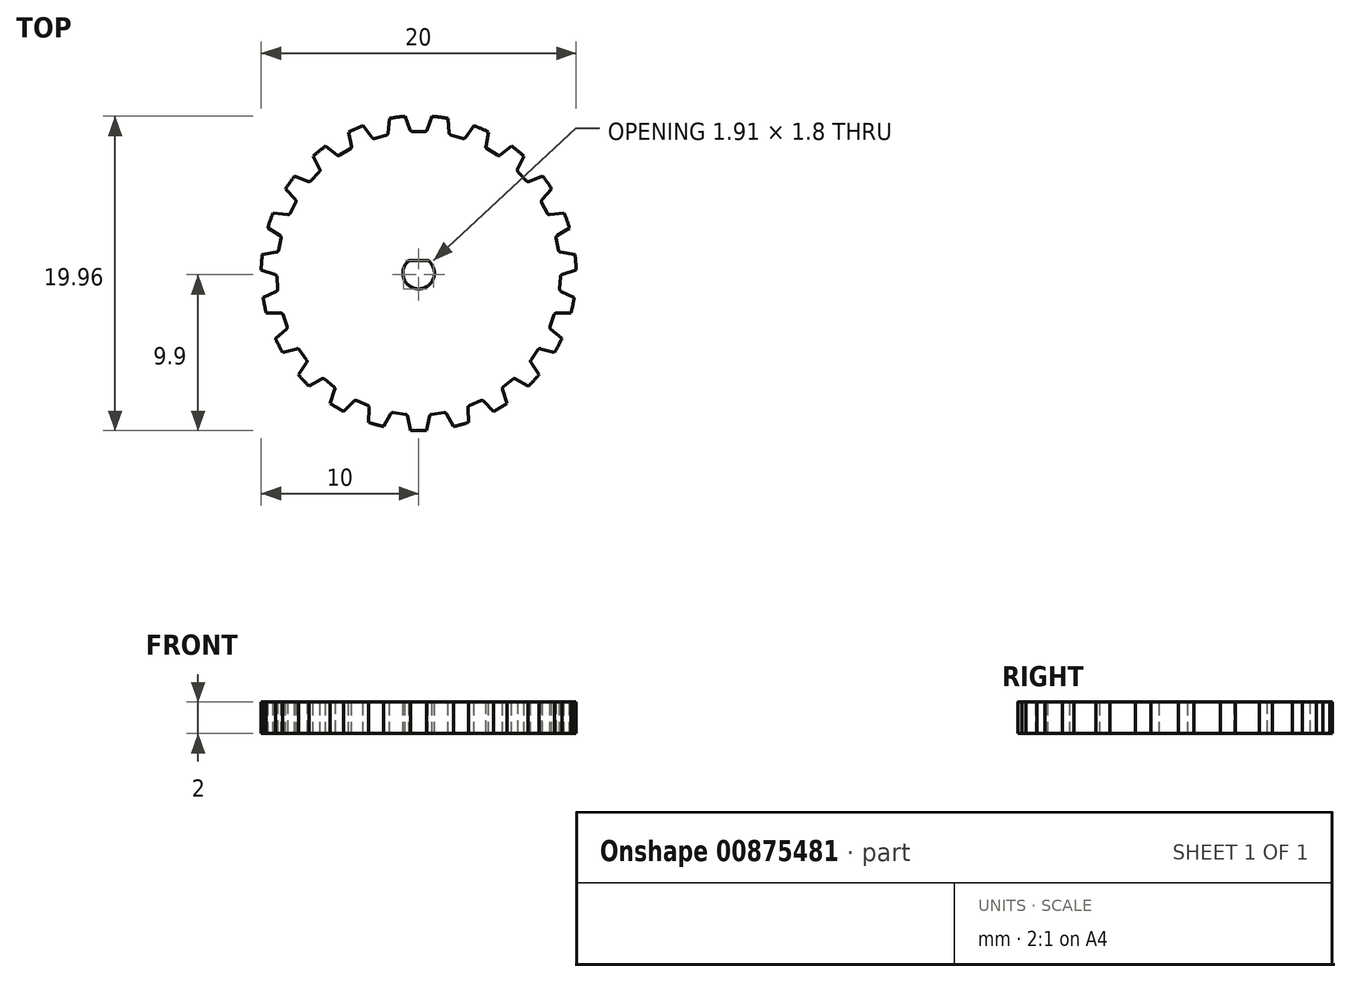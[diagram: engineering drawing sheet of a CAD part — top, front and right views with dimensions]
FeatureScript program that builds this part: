
annotation { "Feature Type Name" : "Feature", "Feature Type Description" : "" }
export const myFeature = defineFeature(function(context is Context, id is Id, definition is map)
    precondition{}
    {
        {
            var Q0;
            Q0=qCreatedBy(makeId("Top.planeOp"),FACE);
            var sketch = newSketch(context, id + "F0", { "sketchPlane" : qUnion([Q0])});
            skCircle(sketch, "E0", {"center": v(0, 0) * mm, "radius": 10 * mm});
            skSolve(sketch);
        }
        {
            var Q0;
            Q0 = qSketchRegion(id + "F0", true);
            extrude(context, id + "F1", {"entities" : qUnion([Q0]), "depth" : 2 * mm, "offsetDistance" : 25 * mm});
        }
        {
            var Q0;
            Q0=makeQuery(id+"F1.opExtrude","CAP_FACE",FACE,{"disambiguationData":[OSD([sQuery(id+"F0.wireOp",EDGE,"E0")])],"isStart":false});
            var sketch = newSketch(context, id + "F2", { "sketchPlane" : qUnion([Q0])});
            skLineSegment(sketch, "E1", {"start": v(0, 0) * mm, "end": v(0, 9) * mm});
            skLineSegment(sketch, "E2", {"start": v(0, 9) * mm, "end": v(0.5, 9) * mm});
            skLineSegment(sketch, "E3", {"start": v(0, 9) * mm, "end": v(0, 10) * mm});
            skLineSegment(sketch, "E4", {"start": v(0, 10) * mm, "end": v(0.88, 10) * mm});
            skLineSegment(sketch, "E5", {"start": v(0.88, 10) * mm, "end": v(0.5, 9) * mm});
            skLineSegment(sketch, "E6.MirrorCS", {"start": v(0, 10) * mm, "end": v(-0.88, 10) * mm});
            skLineSegment(sketch, "E7.MirrorCS", {"start": v(-0.88, 10) * mm, "end": v(-0.5, 9) * mm});
            skLineSegment(sketch, "E8.MirrorCS", {"start": v(0, 9) * mm, "end": v(-0.5, 9) * mm});
            skSolve(sketch);
        }
        {
            var Q0;
            {var subQ0=sQuery(id+"F2.wireOp",EDGE,"E2");Q0=makeQuery(id+"F2.imprint","IMPRINT",FACE,{"disambiguationData":[TD([[makeQuery(id+"F2.imprint","IMPRINT",EDGE,{"derivedFrom":subQ0}),1.0]])]});}
            var Q1;
            {var subQ0=sQuery(id+"F2.wireOp",EDGE,"E3");Q1=makeQuery(id+"F2.imprint","IMPRINT",FACE,{"disambiguationData":[TD([[makeQuery(id+"F2.imprint","IMPRINT",EDGE,{"derivedFrom":subQ0}),1.0]])]});}
            extrude(context, id + "F3", {"entities" : qUnion([Q0, Q1]), "operationType" : NewBodyOperationType.REMOVE, "oppositeDirection" : true, "depth" : 25 * mm, "offsetDistance" : 25 * mm});
        }
        {
            var Q0;
            Q0=makeQuery(id+"F3.boolean.opBoolean","COPY",FACE,{"derivedFrom":makeQuery(id+"F3.opExtrude","SWEPT_FACE",FACE,{"disambiguationData":[OSD([sQuery(id+"F2.wireOp",EDGE,"E5")])]})});
            var Q1;
            Q1=makeQuery(id+"F3.boolean.opBoolean","COPY",FACE,{"derivedFrom":makeQuery(id+"F3.opExtrude","SWEPT_FACE",FACE,{"disambiguationData":[OSD([sQuery(id+"F2.wireOp",EDGE,"E2"),sQuery(id+"F2.wireOp",EDGE,"E8.MirrorCS")])]})});
            var Q2;
            Q2=makeQuery(id+"F3.boolean.opBoolean","COPY",FACE,{"derivedFrom":makeQuery(id+"F3.opExtrude","SWEPT_FACE",FACE,{"disambiguationData":[OSD([sQuery(id+"F2.wireOp",EDGE,"E7.MirrorCS")])]})});
            var Q3;
            Q3=makeQuery(id+"F1.opExtrude","SWEPT_FACE",FACE,{"disambiguationData":[OSD([sQuery(id+"F0.wireOp",EDGE,"E0")])]});
            circularPattern(context, id + "F4", {"patternType" : PatternType.FACE, "faces" : qUnion([Q0, Q1, Q2]), "axis" : qUnion([Q3]), "angle" : 360 * degree, "instanceCount" : 23, "equalSpace" : true});
        }
        {
            var Q0;
            Q0=makeQuery(id+"F3.boolean.opBoolean","COPY",EDGE,{"derivedFrom":makeQuery(id+"F3.opExtrude","SWEPT_EDGE",EDGE,{"disambiguationData":[OSD([sQuery(id+"F2.wireOp",EDGE,"E2"),sQuery(id+"F2.wireOp",EDGE,"E5")])]})});
            var Q1;
            Q1=makeQuery(id+"F3.boolean.opBoolean","COPY",EDGE,{"derivedFrom":makeQuery(id+"F3.opExtrude","SWEPT_EDGE",EDGE,{"disambiguationData":[OSD([sQuery(id+"F2.wireOp",EDGE,"E7.MirrorCS"),sQuery(id+"F2.wireOp",EDGE,"E8.MirrorCS")])]})});
            var Q2;
            Q2=makeQuery(id+"F3.boolean.opBoolean","COPY",EDGE,{"derivedFrom":makeQuery(id+"F3.opExtrude","SWEPT_EDGE",EDGE,{"disambiguationData":[OSD([sQuery(id+"F0.wireOp",EDGE,"E0"),sQuery(id+"F2.wireOp",EDGE,"E5")])]})});
            var Q3;
            Q3=makeQuery(id+"F3.boolean.opBoolean","COPY",EDGE,{"derivedFrom":makeQuery(id+"F3.opExtrude","SWEPT_EDGE",EDGE,{"disambiguationData":[OSD([sQuery(id+"F0.wireOp",EDGE,"E0"),sQuery(id+"F2.wireOp",EDGE,"E7.MirrorCS")])]})});
            fillet(context, id + "F5", {"entities" : qUnion([Q0, Q1, Q2, Q3]), "radius" : .15 * mm, "tangentPropagation" : true, "allowEdgeOverflow" : false});
        }
        {
            var Q0;
            Q0=makeQuery(id+"F4.opPattern","COPY",EDGE,{"derivedFrom":makeQuery(id+"F3.boolean.opBoolean","COPY",EDGE,{"derivedFrom":makeQuery(id+"F3.opExtrude","SWEPT_EDGE",EDGE,{"disambiguationData":[OSD([sQuery(id+"F0.wireOp",EDGE,"E0"),sQuery(id+"F2.wireOp",EDGE,"E5")])]})}),"instanceName":"22"});
            var Q1;
            Q1=makeQuery(id+"F4.opPattern","COPY",EDGE,{"derivedFrom":makeQuery(id+"F3.boolean.opBoolean","COPY",EDGE,{"derivedFrom":makeQuery(id+"F3.opExtrude","SWEPT_EDGE",EDGE,{"disambiguationData":[OSD([sQuery(id+"F2.wireOp",EDGE,"E2"),sQuery(id+"F2.wireOp",EDGE,"E5")])]})}),"instanceName":"22"});
            var Q2;
            Q2=makeQuery(id+"F4.opPattern","COPY",EDGE,{"derivedFrom":makeQuery(id+"F3.boolean.opBoolean","COPY",EDGE,{"derivedFrom":makeQuery(id+"F3.opExtrude","SWEPT_EDGE",EDGE,{"disambiguationData":[OSD([sQuery(id+"F2.wireOp",EDGE,"E7.MirrorCS"),sQuery(id+"F2.wireOp",EDGE,"E8.MirrorCS")])]})}),"instanceName":"22"});
            var Q3;
            Q3=makeQuery(id+"F4.opPattern","COPY",EDGE,{"derivedFrom":makeQuery(id+"F3.boolean.opBoolean","COPY",EDGE,{"derivedFrom":makeQuery(id+"F3.opExtrude","SWEPT_EDGE",EDGE,{"disambiguationData":[OSD([sQuery(id+"F0.wireOp",EDGE,"E0"),sQuery(id+"F2.wireOp",EDGE,"E7.MirrorCS")])]})}),"instanceName":"22"});
            var Q4;
            Q4=makeQuery(id+"F4.opPattern","COPY",EDGE,{"derivedFrom":makeQuery(id+"F3.boolean.opBoolean","COPY",EDGE,{"derivedFrom":makeQuery(id+"F3.opExtrude","SWEPT_EDGE",EDGE,{"disambiguationData":[OSD([sQuery(id+"F0.wireOp",EDGE,"E0"),sQuery(id+"F2.wireOp",EDGE,"E5")])]})}),"instanceName":"21"});
            var Q5;
            Q5=makeQuery(id+"F4.opPattern","COPY",EDGE,{"derivedFrom":makeQuery(id+"F3.boolean.opBoolean","COPY",EDGE,{"derivedFrom":makeQuery(id+"F3.opExtrude","SWEPT_EDGE",EDGE,{"disambiguationData":[OSD([sQuery(id+"F2.wireOp",EDGE,"E2"),sQuery(id+"F2.wireOp",EDGE,"E5")])]})}),"instanceName":"21"});
            var Q6;
            Q6=makeQuery(id+"F4.opPattern","COPY",EDGE,{"derivedFrom":makeQuery(id+"F3.boolean.opBoolean","COPY",EDGE,{"derivedFrom":makeQuery(id+"F3.opExtrude","SWEPT_EDGE",EDGE,{"disambiguationData":[OSD([sQuery(id+"F2.wireOp",EDGE,"E7.MirrorCS"),sQuery(id+"F2.wireOp",EDGE,"E8.MirrorCS")])]})}),"instanceName":"21"});
            var Q7;
            Q7=makeQuery(id+"F4.opPattern","COPY",EDGE,{"derivedFrom":makeQuery(id+"F3.boolean.opBoolean","COPY",EDGE,{"derivedFrom":makeQuery(id+"F3.opExtrude","SWEPT_EDGE",EDGE,{"disambiguationData":[OSD([sQuery(id+"F0.wireOp",EDGE,"E0"),sQuery(id+"F2.wireOp",EDGE,"E7.MirrorCS")])]})}),"instanceName":"21"});
            var Q8;
            Q8=makeQuery(id+"F4.opPattern","COPY",EDGE,{"derivedFrom":makeQuery(id+"F3.boolean.opBoolean","COPY",EDGE,{"derivedFrom":makeQuery(id+"F3.opExtrude","SWEPT_EDGE",EDGE,{"disambiguationData":[OSD([sQuery(id+"F0.wireOp",EDGE,"E0"),sQuery(id+"F2.wireOp",EDGE,"E5")])]})}),"instanceName":"20"});
            var Q9;
            Q9=makeQuery(id+"F4.opPattern","COPY",EDGE,{"derivedFrom":makeQuery(id+"F3.boolean.opBoolean","COPY",EDGE,{"derivedFrom":makeQuery(id+"F3.opExtrude","SWEPT_EDGE",EDGE,{"disambiguationData":[OSD([sQuery(id+"F2.wireOp",EDGE,"E2"),sQuery(id+"F2.wireOp",EDGE,"E5")])]})}),"instanceName":"20"});
            var Q10;
            Q10=makeQuery(id+"F4.opPattern","COPY",EDGE,{"derivedFrom":makeQuery(id+"F3.boolean.opBoolean","COPY",EDGE,{"derivedFrom":makeQuery(id+"F3.opExtrude","SWEPT_EDGE",EDGE,{"disambiguationData":[OSD([sQuery(id+"F2.wireOp",EDGE,"E7.MirrorCS"),sQuery(id+"F2.wireOp",EDGE,"E8.MirrorCS")])]})}),"instanceName":"20"});
            var Q11;
            Q11=makeQuery(id+"F4.opPattern","COPY",EDGE,{"derivedFrom":makeQuery(id+"F3.boolean.opBoolean","COPY",EDGE,{"derivedFrom":makeQuery(id+"F3.opExtrude","SWEPT_EDGE",EDGE,{"disambiguationData":[OSD([sQuery(id+"F0.wireOp",EDGE,"E0"),sQuery(id+"F2.wireOp",EDGE,"E7.MirrorCS")])]})}),"instanceName":"20"});
            var Q12;
            Q12=makeQuery(id+"F4.opPattern","COPY",EDGE,{"derivedFrom":makeQuery(id+"F3.boolean.opBoolean","COPY",EDGE,{"derivedFrom":makeQuery(id+"F3.opExtrude","SWEPT_EDGE",EDGE,{"disambiguationData":[OSD([sQuery(id+"F0.wireOp",EDGE,"E0"),sQuery(id+"F2.wireOp",EDGE,"E5")])]})}),"instanceName":"19"});
            var Q13;
            Q13=makeQuery(id+"F4.opPattern","COPY",EDGE,{"derivedFrom":makeQuery(id+"F3.boolean.opBoolean","COPY",EDGE,{"derivedFrom":makeQuery(id+"F3.opExtrude","SWEPT_EDGE",EDGE,{"disambiguationData":[OSD([sQuery(id+"F2.wireOp",EDGE,"E2"),sQuery(id+"F2.wireOp",EDGE,"E5")])]})}),"instanceName":"19"});
            var Q14;
            Q14=makeQuery(id+"F4.opPattern","COPY",EDGE,{"derivedFrom":makeQuery(id+"F3.boolean.opBoolean","COPY",EDGE,{"derivedFrom":makeQuery(id+"F3.opExtrude","SWEPT_EDGE",EDGE,{"disambiguationData":[OSD([sQuery(id+"F2.wireOp",EDGE,"E7.MirrorCS"),sQuery(id+"F2.wireOp",EDGE,"E8.MirrorCS")])]})}),"instanceName":"19"});
            var Q15;
            Q15=makeQuery(id+"F4.opPattern","COPY",EDGE,{"derivedFrom":makeQuery(id+"F3.boolean.opBoolean","COPY",EDGE,{"derivedFrom":makeQuery(id+"F3.opExtrude","SWEPT_EDGE",EDGE,{"disambiguationData":[OSD([sQuery(id+"F0.wireOp",EDGE,"E0"),sQuery(id+"F2.wireOp",EDGE,"E7.MirrorCS")])]})}),"instanceName":"19"});
            fillet(context, id + "F6", {"entities" : qUnion([Q0, Q1, Q2, Q3, Q4, Q5, Q6, Q7, Q8, Q9, Q10, Q11, Q12, Q13, Q14, Q15]), "radius" : .15 * mm, "tangentPropagation" : true, "allowEdgeOverflow" : false});
        }
        {
            var Q0;
            Q0=makeQuery(id+"F4.opPattern","COPY",EDGE,{"derivedFrom":makeQuery(id+"F3.boolean.opBoolean","COPY",EDGE,{"derivedFrom":makeQuery(id+"F3.opExtrude","SWEPT_EDGE",EDGE,{"disambiguationData":[OSD([sQuery(id+"F0.wireOp",EDGE,"E0"),sQuery(id+"F2.wireOp",EDGE,"E7.MirrorCS")])]})}),"instanceName":"1"});
            var Q1;
            Q1=makeQuery(id+"F4.opPattern","COPY",EDGE,{"derivedFrom":makeQuery(id+"F3.boolean.opBoolean","COPY",EDGE,{"derivedFrom":makeQuery(id+"F3.opExtrude","SWEPT_EDGE",EDGE,{"disambiguationData":[OSD([sQuery(id+"F2.wireOp",EDGE,"E7.MirrorCS"),sQuery(id+"F2.wireOp",EDGE,"E8.MirrorCS")])]})}),"instanceName":"1"});
            var Q2;
            Q2=makeQuery(id+"F4.opPattern","COPY",EDGE,{"derivedFrom":makeQuery(id+"F3.boolean.opBoolean","COPY",EDGE,{"derivedFrom":makeQuery(id+"F3.opExtrude","SWEPT_EDGE",EDGE,{"disambiguationData":[OSD([sQuery(id+"F2.wireOp",EDGE,"E2"),sQuery(id+"F2.wireOp",EDGE,"E5")])]})}),"instanceName":"1"});
            var Q3;
            Q3=makeQuery(id+"F4.opPattern","COPY",EDGE,{"derivedFrom":makeQuery(id+"F3.boolean.opBoolean","COPY",EDGE,{"derivedFrom":makeQuery(id+"F3.opExtrude","SWEPT_EDGE",EDGE,{"disambiguationData":[OSD([sQuery(id+"F0.wireOp",EDGE,"E0"),sQuery(id+"F2.wireOp",EDGE,"E5")])]})}),"instanceName":"1"});
            var Q4;
            Q4=makeQuery(id+"F4.opPattern","COPY",EDGE,{"derivedFrom":makeQuery(id+"F3.boolean.opBoolean","COPY",EDGE,{"derivedFrom":makeQuery(id+"F3.opExtrude","SWEPT_EDGE",EDGE,{"disambiguationData":[OSD([sQuery(id+"F0.wireOp",EDGE,"E0"),sQuery(id+"F2.wireOp",EDGE,"E7.MirrorCS")])]})}),"instanceName":"2"});
            var Q5;
            Q5=makeQuery(id+"F4.opPattern","COPY",EDGE,{"derivedFrom":makeQuery(id+"F3.boolean.opBoolean","COPY",EDGE,{"derivedFrom":makeQuery(id+"F3.opExtrude","SWEPT_EDGE",EDGE,{"disambiguationData":[OSD([sQuery(id+"F2.wireOp",EDGE,"E2"),sQuery(id+"F2.wireOp",EDGE,"E5")])]})}),"instanceName":"2"});
            var Q6;
            Q6=makeQuery(id+"F4.opPattern","COPY",EDGE,{"derivedFrom":makeQuery(id+"F3.boolean.opBoolean","COPY",EDGE,{"derivedFrom":makeQuery(id+"F3.opExtrude","SWEPT_EDGE",EDGE,{"disambiguationData":[OSD([sQuery(id+"F2.wireOp",EDGE,"E7.MirrorCS"),sQuery(id+"F2.wireOp",EDGE,"E8.MirrorCS")])]})}),"instanceName":"2"});
            var Q7;
            Q7=makeQuery(id+"F4.opPattern","COPY",EDGE,{"derivedFrom":makeQuery(id+"F3.boolean.opBoolean","COPY",EDGE,{"derivedFrom":makeQuery(id+"F3.opExtrude","SWEPT_EDGE",EDGE,{"disambiguationData":[OSD([sQuery(id+"F0.wireOp",EDGE,"E0"),sQuery(id+"F2.wireOp",EDGE,"E5")])]})}),"instanceName":"2"});
            var Q8;
            Q8=makeQuery(id+"F4.opPattern","COPY",EDGE,{"derivedFrom":makeQuery(id+"F3.boolean.opBoolean","COPY",EDGE,{"derivedFrom":makeQuery(id+"F3.opExtrude","SWEPT_EDGE",EDGE,{"disambiguationData":[OSD([sQuery(id+"F0.wireOp",EDGE,"E0"),sQuery(id+"F2.wireOp",EDGE,"E7.MirrorCS")])]})}),"instanceName":"3"});
            var Q9;
            Q9=makeQuery(id+"F4.opPattern","COPY",EDGE,{"derivedFrom":makeQuery(id+"F3.boolean.opBoolean","COPY",EDGE,{"derivedFrom":makeQuery(id+"F3.opExtrude","SWEPT_EDGE",EDGE,{"disambiguationData":[OSD([sQuery(id+"F2.wireOp",EDGE,"E7.MirrorCS"),sQuery(id+"F2.wireOp",EDGE,"E8.MirrorCS")])]})}),"instanceName":"3"});
            var Q10;
            Q10=makeQuery(id+"F4.opPattern","COPY",EDGE,{"derivedFrom":makeQuery(id+"F3.boolean.opBoolean","COPY",EDGE,{"derivedFrom":makeQuery(id+"F3.opExtrude","SWEPT_EDGE",EDGE,{"disambiguationData":[OSD([sQuery(id+"F2.wireOp",EDGE,"E2"),sQuery(id+"F2.wireOp",EDGE,"E5")])]})}),"instanceName":"3"});
            var Q11;
            Q11=makeQuery(id+"F4.opPattern","COPY",EDGE,{"derivedFrom":makeQuery(id+"F3.boolean.opBoolean","COPY",EDGE,{"derivedFrom":makeQuery(id+"F3.opExtrude","SWEPT_EDGE",EDGE,{"disambiguationData":[OSD([sQuery(id+"F0.wireOp",EDGE,"E0"),sQuery(id+"F2.wireOp",EDGE,"E5")])]})}),"instanceName":"3"});
            var Q12;
            Q12=makeQuery(id+"F4.opPattern","COPY",EDGE,{"derivedFrom":makeQuery(id+"F3.boolean.opBoolean","COPY",EDGE,{"derivedFrom":makeQuery(id+"F3.opExtrude","SWEPT_EDGE",EDGE,{"disambiguationData":[OSD([sQuery(id+"F0.wireOp",EDGE,"E0"),sQuery(id+"F2.wireOp",EDGE,"E7.MirrorCS")])]})}),"instanceName":"4"});
            var Q13;
            Q13=makeQuery(id+"F4.opPattern","COPY",EDGE,{"derivedFrom":makeQuery(id+"F3.boolean.opBoolean","COPY",EDGE,{"derivedFrom":makeQuery(id+"F3.opExtrude","SWEPT_EDGE",EDGE,{"disambiguationData":[OSD([sQuery(id+"F2.wireOp",EDGE,"E7.MirrorCS"),sQuery(id+"F2.wireOp",EDGE,"E8.MirrorCS")])]})}),"instanceName":"4"});
            var Q14;
            Q14=makeQuery(id+"F4.opPattern","COPY",EDGE,{"derivedFrom":makeQuery(id+"F3.boolean.opBoolean","COPY",EDGE,{"derivedFrom":makeQuery(id+"F3.opExtrude","SWEPT_EDGE",EDGE,{"disambiguationData":[OSD([sQuery(id+"F2.wireOp",EDGE,"E2"),sQuery(id+"F2.wireOp",EDGE,"E5")])]})}),"instanceName":"4"});
            var Q15;
            Q15=makeQuery(id+"F4.opPattern","COPY",EDGE,{"derivedFrom":makeQuery(id+"F3.boolean.opBoolean","COPY",EDGE,{"derivedFrom":makeQuery(id+"F3.opExtrude","SWEPT_EDGE",EDGE,{"disambiguationData":[OSD([sQuery(id+"F0.wireOp",EDGE,"E0"),sQuery(id+"F2.wireOp",EDGE,"E5")])]})}),"instanceName":"4"});
            var Q16;
            Q16=makeQuery(id+"F4.opPattern","COPY",EDGE,{"derivedFrom":makeQuery(id+"F3.boolean.opBoolean","COPY",EDGE,{"derivedFrom":makeQuery(id+"F3.opExtrude","SWEPT_EDGE",EDGE,{"disambiguationData":[OSD([sQuery(id+"F0.wireOp",EDGE,"E0"),sQuery(id+"F2.wireOp",EDGE,"E7.MirrorCS")])]})}),"instanceName":"5"});
            var Q17;
            Q17=makeQuery(id+"F4.opPattern","COPY",EDGE,{"derivedFrom":makeQuery(id+"F3.boolean.opBoolean","COPY",EDGE,{"derivedFrom":makeQuery(id+"F3.opExtrude","SWEPT_EDGE",EDGE,{"disambiguationData":[OSD([sQuery(id+"F2.wireOp",EDGE,"E7.MirrorCS"),sQuery(id+"F2.wireOp",EDGE,"E8.MirrorCS")])]})}),"instanceName":"5"});
            var Q18;
            Q18=makeQuery(id+"F4.opPattern","COPY",EDGE,{"derivedFrom":makeQuery(id+"F3.boolean.opBoolean","COPY",EDGE,{"derivedFrom":makeQuery(id+"F3.opExtrude","SWEPT_EDGE",EDGE,{"disambiguationData":[OSD([sQuery(id+"F2.wireOp",EDGE,"E2"),sQuery(id+"F2.wireOp",EDGE,"E5")])]})}),"instanceName":"5"});
            var Q19;
            Q19=makeQuery(id+"F4.opPattern","COPY",EDGE,{"derivedFrom":makeQuery(id+"F3.boolean.opBoolean","COPY",EDGE,{"derivedFrom":makeQuery(id+"F3.opExtrude","SWEPT_EDGE",EDGE,{"disambiguationData":[OSD([sQuery(id+"F0.wireOp",EDGE,"E0"),sQuery(id+"F2.wireOp",EDGE,"E5")])]})}),"instanceName":"5"});
            var Q20;
            Q20=makeQuery(id+"F4.opPattern","COPY",EDGE,{"derivedFrom":makeQuery(id+"F3.boolean.opBoolean","COPY",EDGE,{"derivedFrom":makeQuery(id+"F3.opExtrude","SWEPT_EDGE",EDGE,{"disambiguationData":[OSD([sQuery(id+"F0.wireOp",EDGE,"E0"),sQuery(id+"F2.wireOp",EDGE,"E7.MirrorCS")])]})}),"instanceName":"6"});
            var Q21;
            Q21=makeQuery(id+"F4.opPattern","COPY",EDGE,{"derivedFrom":makeQuery(id+"F3.boolean.opBoolean","COPY",EDGE,{"derivedFrom":makeQuery(id+"F3.opExtrude","SWEPT_EDGE",EDGE,{"disambiguationData":[OSD([sQuery(id+"F2.wireOp",EDGE,"E7.MirrorCS"),sQuery(id+"F2.wireOp",EDGE,"E8.MirrorCS")])]})}),"instanceName":"6"});
            var Q22;
            Q22=makeQuery(id+"F4.opPattern","COPY",EDGE,{"derivedFrom":makeQuery(id+"F3.boolean.opBoolean","COPY",EDGE,{"derivedFrom":makeQuery(id+"F3.opExtrude","SWEPT_EDGE",EDGE,{"disambiguationData":[OSD([sQuery(id+"F2.wireOp",EDGE,"E2"),sQuery(id+"F2.wireOp",EDGE,"E5")])]})}),"instanceName":"6"});
            var Q23;
            Q23=makeQuery(id+"F4.opPattern","COPY",EDGE,{"derivedFrom":makeQuery(id+"F3.boolean.opBoolean","COPY",EDGE,{"derivedFrom":makeQuery(id+"F3.opExtrude","SWEPT_EDGE",EDGE,{"disambiguationData":[OSD([sQuery(id+"F0.wireOp",EDGE,"E0"),sQuery(id+"F2.wireOp",EDGE,"E5")])]})}),"instanceName":"6"});
            var Q24;
            Q24=makeQuery(id+"F4.opPattern","COPY",EDGE,{"derivedFrom":makeQuery(id+"F3.boolean.opBoolean","COPY",EDGE,{"derivedFrom":makeQuery(id+"F3.opExtrude","SWEPT_EDGE",EDGE,{"disambiguationData":[OSD([sQuery(id+"F0.wireOp",EDGE,"E0"),sQuery(id+"F2.wireOp",EDGE,"E7.MirrorCS")])]})}),"instanceName":"7"});
            var Q25;
            Q25=makeQuery(id+"F4.opPattern","COPY",EDGE,{"derivedFrom":makeQuery(id+"F3.boolean.opBoolean","COPY",EDGE,{"derivedFrom":makeQuery(id+"F3.opExtrude","SWEPT_EDGE",EDGE,{"disambiguationData":[OSD([sQuery(id+"F2.wireOp",EDGE,"E7.MirrorCS"),sQuery(id+"F2.wireOp",EDGE,"E8.MirrorCS")])]})}),"instanceName":"7"});
            fillet(context, id + "F7", {"entities" : qUnion([Q0, Q1, Q2, Q3, Q4, Q5, Q6, Q7, Q8, Q9, Q10, Q11, Q12, Q13, Q14, Q15, Q16, Q17, Q18, Q19, Q20, Q21, Q22, Q23, Q24, Q25]), "radius" : .15 * mm, "tangentPropagation" : true, "allowEdgeOverflow" : false});
        }
        {
            var Q0;
            Q0=makeQuery(id+"F4.opPattern","COPY",EDGE,{"derivedFrom":makeQuery(id+"F3.boolean.opBoolean","COPY",EDGE,{"derivedFrom":makeQuery(id+"F3.opExtrude","SWEPT_EDGE",EDGE,{"disambiguationData":[OSD([sQuery(id+"F2.wireOp",EDGE,"E2"),sQuery(id+"F2.wireOp",EDGE,"E5")])]})}),"instanceName":"7"});
            var Q1;
            Q1=makeQuery(id+"F4.opPattern","COPY",EDGE,{"derivedFrom":makeQuery(id+"F3.boolean.opBoolean","COPY",EDGE,{"derivedFrom":makeQuery(id+"F3.opExtrude","SWEPT_EDGE",EDGE,{"disambiguationData":[OSD([sQuery(id+"F0.wireOp",EDGE,"E0"),sQuery(id+"F2.wireOp",EDGE,"E5")])]})}),"instanceName":"7"});
            var Q2;
            Q2=makeQuery(id+"F4.opPattern","COPY",EDGE,{"derivedFrom":makeQuery(id+"F3.boolean.opBoolean","COPY",EDGE,{"derivedFrom":makeQuery(id+"F3.opExtrude","SWEPT_EDGE",EDGE,{"disambiguationData":[OSD([sQuery(id+"F0.wireOp",EDGE,"E0"),sQuery(id+"F2.wireOp",EDGE,"E7.MirrorCS")])]})}),"instanceName":"8"});
            var Q3;
            Q3=makeQuery(id+"F4.opPattern","COPY",EDGE,{"derivedFrom":makeQuery(id+"F3.boolean.opBoolean","COPY",EDGE,{"derivedFrom":makeQuery(id+"F3.opExtrude","SWEPT_EDGE",EDGE,{"disambiguationData":[OSD([sQuery(id+"F2.wireOp",EDGE,"E7.MirrorCS"),sQuery(id+"F2.wireOp",EDGE,"E8.MirrorCS")])]})}),"instanceName":"8"});
            var Q4;
            Q4=makeQuery(id+"F4.opPattern","COPY",EDGE,{"derivedFrom":makeQuery(id+"F3.boolean.opBoolean","COPY",EDGE,{"derivedFrom":makeQuery(id+"F3.opExtrude","SWEPT_EDGE",EDGE,{"disambiguationData":[OSD([sQuery(id+"F2.wireOp",EDGE,"E2"),sQuery(id+"F2.wireOp",EDGE,"E5")])]})}),"instanceName":"8"});
            var Q5;
            Q5=makeQuery(id+"F4.opPattern","COPY",EDGE,{"derivedFrom":makeQuery(id+"F3.boolean.opBoolean","COPY",EDGE,{"derivedFrom":makeQuery(id+"F3.opExtrude","SWEPT_EDGE",EDGE,{"disambiguationData":[OSD([sQuery(id+"F0.wireOp",EDGE,"E0"),sQuery(id+"F2.wireOp",EDGE,"E5")])]})}),"instanceName":"8"});
            var Q6;
            Q6=makeQuery(id+"F4.opPattern","COPY",EDGE,{"derivedFrom":makeQuery(id+"F3.boolean.opBoolean","COPY",EDGE,{"derivedFrom":makeQuery(id+"F3.opExtrude","SWEPT_EDGE",EDGE,{"disambiguationData":[OSD([sQuery(id+"F0.wireOp",EDGE,"E0"),sQuery(id+"F2.wireOp",EDGE,"E7.MirrorCS")])]})}),"instanceName":"9"});
            var Q7;
            Q7=makeQuery(id+"F4.opPattern","COPY",EDGE,{"derivedFrom":makeQuery(id+"F3.boolean.opBoolean","COPY",EDGE,{"derivedFrom":makeQuery(id+"F3.opExtrude","SWEPT_EDGE",EDGE,{"disambiguationData":[OSD([sQuery(id+"F2.wireOp",EDGE,"E7.MirrorCS"),sQuery(id+"F2.wireOp",EDGE,"E8.MirrorCS")])]})}),"instanceName":"9"});
            var Q8;
            Q8=makeQuery(id+"F4.opPattern","COPY",EDGE,{"derivedFrom":makeQuery(id+"F3.boolean.opBoolean","COPY",EDGE,{"derivedFrom":makeQuery(id+"F3.opExtrude","SWEPT_EDGE",EDGE,{"disambiguationData":[OSD([sQuery(id+"F2.wireOp",EDGE,"E2"),sQuery(id+"F2.wireOp",EDGE,"E5")])]})}),"instanceName":"9"});
            var Q9;
            Q9=makeQuery(id+"F4.opPattern","COPY",EDGE,{"derivedFrom":makeQuery(id+"F3.boolean.opBoolean","COPY",EDGE,{"derivedFrom":makeQuery(id+"F3.opExtrude","SWEPT_EDGE",EDGE,{"disambiguationData":[OSD([sQuery(id+"F0.wireOp",EDGE,"E0"),sQuery(id+"F2.wireOp",EDGE,"E5")])]})}),"instanceName":"9"});
            var Q10;
            Q10=makeQuery(id+"F4.opPattern","COPY",EDGE,{"derivedFrom":makeQuery(id+"F3.boolean.opBoolean","COPY",EDGE,{"derivedFrom":makeQuery(id+"F3.opExtrude","SWEPT_EDGE",EDGE,{"disambiguationData":[OSD([sQuery(id+"F0.wireOp",EDGE,"E0"),sQuery(id+"F2.wireOp",EDGE,"E7.MirrorCS")])]})}),"instanceName":"10"});
            var Q11;
            Q11=makeQuery(id+"F4.opPattern","COPY",EDGE,{"derivedFrom":makeQuery(id+"F3.boolean.opBoolean","COPY",EDGE,{"derivedFrom":makeQuery(id+"F3.opExtrude","SWEPT_EDGE",EDGE,{"disambiguationData":[OSD([sQuery(id+"F2.wireOp",EDGE,"E7.MirrorCS"),sQuery(id+"F2.wireOp",EDGE,"E8.MirrorCS")])]})}),"instanceName":"10"});
            var Q12;
            Q12=makeQuery(id+"F4.opPattern","COPY",EDGE,{"derivedFrom":makeQuery(id+"F3.boolean.opBoolean","COPY",EDGE,{"derivedFrom":makeQuery(id+"F3.opExtrude","SWEPT_EDGE",EDGE,{"disambiguationData":[OSD([sQuery(id+"F2.wireOp",EDGE,"E2"),sQuery(id+"F2.wireOp",EDGE,"E5")])]})}),"instanceName":"10"});
            var Q13;
            Q13=makeQuery(id+"F4.opPattern","COPY",EDGE,{"derivedFrom":makeQuery(id+"F3.boolean.opBoolean","COPY",EDGE,{"derivedFrom":makeQuery(id+"F3.opExtrude","SWEPT_EDGE",EDGE,{"disambiguationData":[OSD([sQuery(id+"F0.wireOp",EDGE,"E0"),sQuery(id+"F2.wireOp",EDGE,"E5")])]})}),"instanceName":"10"});
            var Q14;
            Q14=makeQuery(id+"F4.opPattern","COPY",EDGE,{"derivedFrom":makeQuery(id+"F3.boolean.opBoolean","COPY",EDGE,{"derivedFrom":makeQuery(id+"F3.opExtrude","SWEPT_EDGE",EDGE,{"disambiguationData":[OSD([sQuery(id+"F0.wireOp",EDGE,"E0"),sQuery(id+"F2.wireOp",EDGE,"E7.MirrorCS")])]})}),"instanceName":"11"});
            var Q15;
            Q15=makeQuery(id+"F4.opPattern","COPY",EDGE,{"derivedFrom":makeQuery(id+"F3.boolean.opBoolean","COPY",EDGE,{"derivedFrom":makeQuery(id+"F3.opExtrude","SWEPT_EDGE",EDGE,{"disambiguationData":[OSD([sQuery(id+"F2.wireOp",EDGE,"E7.MirrorCS"),sQuery(id+"F2.wireOp",EDGE,"E8.MirrorCS")])]})}),"instanceName":"11"});
            var Q16;
            Q16=makeQuery(id+"F4.opPattern","COPY",EDGE,{"derivedFrom":makeQuery(id+"F3.boolean.opBoolean","COPY",EDGE,{"derivedFrom":makeQuery(id+"F3.opExtrude","SWEPT_EDGE",EDGE,{"disambiguationData":[OSD([sQuery(id+"F0.wireOp",EDGE,"E0"),sQuery(id+"F2.wireOp",EDGE,"E5")])]})}),"instanceName":"11"});
            var Q17;
            Q17=makeQuery(id+"F4.opPattern","COPY",EDGE,{"derivedFrom":makeQuery(id+"F3.boolean.opBoolean","COPY",EDGE,{"derivedFrom":makeQuery(id+"F3.opExtrude","SWEPT_EDGE",EDGE,{"disambiguationData":[OSD([sQuery(id+"F2.wireOp",EDGE,"E2"),sQuery(id+"F2.wireOp",EDGE,"E5")])]})}),"instanceName":"11"});
            var Q18;
            Q18=makeQuery(id+"F4.opPattern","COPY",EDGE,{"derivedFrom":makeQuery(id+"F3.boolean.opBoolean","COPY",EDGE,{"derivedFrom":makeQuery(id+"F3.opExtrude","SWEPT_EDGE",EDGE,{"disambiguationData":[OSD([sQuery(id+"F0.wireOp",EDGE,"E0"),sQuery(id+"F2.wireOp",EDGE,"E7.MirrorCS")])]})}),"instanceName":"12"});
            var Q19;
            Q19=makeQuery(id+"F4.opPattern","COPY",EDGE,{"derivedFrom":makeQuery(id+"F3.boolean.opBoolean","COPY",EDGE,{"derivedFrom":makeQuery(id+"F3.opExtrude","SWEPT_EDGE",EDGE,{"disambiguationData":[OSD([sQuery(id+"F2.wireOp",EDGE,"E7.MirrorCS"),sQuery(id+"F2.wireOp",EDGE,"E8.MirrorCS")])]})}),"instanceName":"12"});
            var Q20;
            Q20=makeQuery(id+"F4.opPattern","COPY",EDGE,{"derivedFrom":makeQuery(id+"F3.boolean.opBoolean","COPY",EDGE,{"derivedFrom":makeQuery(id+"F3.opExtrude","SWEPT_EDGE",EDGE,{"disambiguationData":[OSD([sQuery(id+"F2.wireOp",EDGE,"E2"),sQuery(id+"F2.wireOp",EDGE,"E5")])]})}),"instanceName":"12"});
            var Q21;
            Q21=makeQuery(id+"F4.opPattern","COPY",EDGE,{"derivedFrom":makeQuery(id+"F3.boolean.opBoolean","COPY",EDGE,{"derivedFrom":makeQuery(id+"F3.opExtrude","SWEPT_EDGE",EDGE,{"disambiguationData":[OSD([sQuery(id+"F0.wireOp",EDGE,"E0"),sQuery(id+"F2.wireOp",EDGE,"E5")])]})}),"instanceName":"12"});
            var Q22;
            Q22=makeQuery(id+"F4.opPattern","COPY",EDGE,{"derivedFrom":makeQuery(id+"F3.boolean.opBoolean","COPY",EDGE,{"derivedFrom":makeQuery(id+"F3.opExtrude","SWEPT_EDGE",EDGE,{"disambiguationData":[OSD([sQuery(id+"F0.wireOp",EDGE,"E0"),sQuery(id+"F2.wireOp",EDGE,"E7.MirrorCS")])]})}),"instanceName":"13"});
            var Q23;
            Q23=makeQuery(id+"F4.opPattern","COPY",EDGE,{"derivedFrom":makeQuery(id+"F3.boolean.opBoolean","COPY",EDGE,{"derivedFrom":makeQuery(id+"F3.opExtrude","SWEPT_EDGE",EDGE,{"disambiguationData":[OSD([sQuery(id+"F2.wireOp",EDGE,"E7.MirrorCS"),sQuery(id+"F2.wireOp",EDGE,"E8.MirrorCS")])]})}),"instanceName":"13"});
            var Q24;
            Q24=makeQuery(id+"F4.opPattern","COPY",EDGE,{"derivedFrom":makeQuery(id+"F3.boolean.opBoolean","COPY",EDGE,{"derivedFrom":makeQuery(id+"F3.opExtrude","SWEPT_EDGE",EDGE,{"disambiguationData":[OSD([sQuery(id+"F0.wireOp",EDGE,"E0"),sQuery(id+"F2.wireOp",EDGE,"E5")])]})}),"instanceName":"13"});
            var Q25;
            Q25=makeQuery(id+"F4.opPattern","COPY",EDGE,{"derivedFrom":makeQuery(id+"F3.boolean.opBoolean","COPY",EDGE,{"derivedFrom":makeQuery(id+"F3.opExtrude","SWEPT_EDGE",EDGE,{"disambiguationData":[OSD([sQuery(id+"F0.wireOp",EDGE,"E0"),sQuery(id+"F2.wireOp",EDGE,"E7.MirrorCS")])]})}),"instanceName":"14"});
            var Q26;
            Q26=makeQuery(id+"F4.opPattern","COPY",EDGE,{"derivedFrom":makeQuery(id+"F3.boolean.opBoolean","COPY",EDGE,{"derivedFrom":makeQuery(id+"F3.opExtrude","SWEPT_EDGE",EDGE,{"disambiguationData":[OSD([sQuery(id+"F2.wireOp",EDGE,"E7.MirrorCS"),sQuery(id+"F2.wireOp",EDGE,"E8.MirrorCS")])]})}),"instanceName":"14"});
            var Q27;
            Q27=makeQuery(id+"F4.opPattern","COPY",EDGE,{"derivedFrom":makeQuery(id+"F3.boolean.opBoolean","COPY",EDGE,{"derivedFrom":makeQuery(id+"F3.opExtrude","SWEPT_EDGE",EDGE,{"disambiguationData":[OSD([sQuery(id+"F2.wireOp",EDGE,"E2"),sQuery(id+"F2.wireOp",EDGE,"E5")])]})}),"instanceName":"14"});
            var Q28;
            Q28=makeQuery(id+"F4.opPattern","COPY",EDGE,{"derivedFrom":makeQuery(id+"F3.boolean.opBoolean","COPY",EDGE,{"derivedFrom":makeQuery(id+"F3.opExtrude","SWEPT_EDGE",EDGE,{"disambiguationData":[OSD([sQuery(id+"F0.wireOp",EDGE,"E0"),sQuery(id+"F2.wireOp",EDGE,"E5")])]})}),"instanceName":"14"});
            var Q29;
            Q29=makeQuery(id+"F4.opPattern","COPY",EDGE,{"derivedFrom":makeQuery(id+"F3.boolean.opBoolean","COPY",EDGE,{"derivedFrom":makeQuery(id+"F3.opExtrude","SWEPT_EDGE",EDGE,{"disambiguationData":[OSD([sQuery(id+"F0.wireOp",EDGE,"E0"),sQuery(id+"F2.wireOp",EDGE,"E7.MirrorCS")])]})}),"instanceName":"15"});
            var Q30;
            Q30=makeQuery(id+"F4.opPattern","COPY",EDGE,{"derivedFrom":makeQuery(id+"F3.boolean.opBoolean","COPY",EDGE,{"derivedFrom":makeQuery(id+"F3.opExtrude","SWEPT_EDGE",EDGE,{"disambiguationData":[OSD([sQuery(id+"F2.wireOp",EDGE,"E2"),sQuery(id+"F2.wireOp",EDGE,"E5")])]})}),"instanceName":"15"});
            var Q31;
            Q31=makeQuery(id+"F4.opPattern","COPY",EDGE,{"derivedFrom":makeQuery(id+"F3.boolean.opBoolean","COPY",EDGE,{"derivedFrom":makeQuery(id+"F3.opExtrude","SWEPT_EDGE",EDGE,{"disambiguationData":[OSD([sQuery(id+"F0.wireOp",EDGE,"E0"),sQuery(id+"F2.wireOp",EDGE,"E5")])]})}),"instanceName":"15"});
            var Q32;
            Q32=makeQuery(id+"F4.opPattern","COPY",EDGE,{"derivedFrom":makeQuery(id+"F3.boolean.opBoolean","COPY",EDGE,{"derivedFrom":makeQuery(id+"F3.opExtrude","SWEPT_EDGE",EDGE,{"disambiguationData":[OSD([sQuery(id+"F2.wireOp",EDGE,"E2"),sQuery(id+"F2.wireOp",EDGE,"E5")])]})}),"instanceName":"16"});
            var Q33;
            Q33=makeQuery(id+"F4.opPattern","COPY",EDGE,{"derivedFrom":makeQuery(id+"F3.boolean.opBoolean","COPY",EDGE,{"derivedFrom":makeQuery(id+"F3.opExtrude","SWEPT_EDGE",EDGE,{"disambiguationData":[OSD([sQuery(id+"F0.wireOp",EDGE,"E0"),sQuery(id+"F2.wireOp",EDGE,"E5")])]})}),"instanceName":"16"});
            var Q34;
            Q34=makeQuery(id+"F4.opPattern","COPY",EDGE,{"derivedFrom":makeQuery(id+"F3.boolean.opBoolean","COPY",EDGE,{"derivedFrom":makeQuery(id+"F3.opExtrude","SWEPT_EDGE",EDGE,{"disambiguationData":[OSD([sQuery(id+"F2.wireOp",EDGE,"E2"),sQuery(id+"F2.wireOp",EDGE,"E5")])]})}),"instanceName":"17"});
            var Q35;
            Q35=makeQuery(id+"F4.opPattern","COPY",EDGE,{"derivedFrom":makeQuery(id+"F3.boolean.opBoolean","COPY",EDGE,{"derivedFrom":makeQuery(id+"F3.opExtrude","SWEPT_EDGE",EDGE,{"disambiguationData":[OSD([sQuery(id+"F0.wireOp",EDGE,"E0"),sQuery(id+"F2.wireOp",EDGE,"E5")])]})}),"instanceName":"17"});
            var Q36;
            Q36=makeQuery(id+"F4.opPattern","COPY",EDGE,{"derivedFrom":makeQuery(id+"F3.boolean.opBoolean","COPY",EDGE,{"derivedFrom":makeQuery(id+"F3.opExtrude","SWEPT_EDGE",EDGE,{"disambiguationData":[OSD([sQuery(id+"F0.wireOp",EDGE,"E0"),sQuery(id+"F2.wireOp",EDGE,"E7.MirrorCS")])]})}),"instanceName":"18"});
            var Q37;
            Q37=makeQuery(id+"F4.opPattern","COPY",EDGE,{"derivedFrom":makeQuery(id+"F3.boolean.opBoolean","COPY",EDGE,{"derivedFrom":makeQuery(id+"F3.opExtrude","SWEPT_EDGE",EDGE,{"disambiguationData":[OSD([sQuery(id+"F0.wireOp",EDGE,"E0"),sQuery(id+"F2.wireOp",EDGE,"E7.MirrorCS")])]})}),"instanceName":"16"});
            var Q38;
            Q38=makeQuery(id+"F4.opPattern","COPY",EDGE,{"derivedFrom":makeQuery(id+"F3.boolean.opBoolean","COPY",EDGE,{"derivedFrom":makeQuery(id+"F3.opExtrude","SWEPT_EDGE",EDGE,{"disambiguationData":[OSD([sQuery(id+"F0.wireOp",EDGE,"E0"),sQuery(id+"F2.wireOp",EDGE,"E7.MirrorCS")])]})}),"instanceName":"17"});
            var Q39;
            Q39=makeQuery(id+"F4.opPattern","COPY",EDGE,{"derivedFrom":makeQuery(id+"F3.boolean.opBoolean","COPY",EDGE,{"derivedFrom":makeQuery(id+"F3.opExtrude","SWEPT_EDGE",EDGE,{"disambiguationData":[OSD([sQuery(id+"F2.wireOp",EDGE,"E7.MirrorCS"),sQuery(id+"F2.wireOp",EDGE,"E8.MirrorCS")])]})}),"instanceName":"15"});
            var Q40;
            Q40=makeQuery(id+"F4.opPattern","COPY",EDGE,{"derivedFrom":makeQuery(id+"F3.boolean.opBoolean","COPY",EDGE,{"derivedFrom":makeQuery(id+"F3.opExtrude","SWEPT_EDGE",EDGE,{"disambiguationData":[OSD([sQuery(id+"F2.wireOp",EDGE,"E2"),sQuery(id+"F2.wireOp",EDGE,"E5")])]})}),"instanceName":"13"});
            var Q41;
            Q41=makeQuery(id+"F4.opPattern","COPY",EDGE,{"derivedFrom":makeQuery(id+"F3.boolean.opBoolean","COPY",EDGE,{"derivedFrom":makeQuery(id+"F3.opExtrude","SWEPT_EDGE",EDGE,{"disambiguationData":[OSD([sQuery(id+"F2.wireOp",EDGE,"E7.MirrorCS"),sQuery(id+"F2.wireOp",EDGE,"E8.MirrorCS")])]})}),"instanceName":"16"});
            var Q42;
            Q42=makeQuery(id+"F4.opPattern","COPY",EDGE,{"derivedFrom":makeQuery(id+"F3.boolean.opBoolean","COPY",EDGE,{"derivedFrom":makeQuery(id+"F3.opExtrude","SWEPT_EDGE",EDGE,{"disambiguationData":[OSD([sQuery(id+"F2.wireOp",EDGE,"E7.MirrorCS"),sQuery(id+"F2.wireOp",EDGE,"E8.MirrorCS")])]})}),"instanceName":"17"});
            var Q43;
            Q43=makeQuery(id+"F4.opPattern","COPY",EDGE,{"derivedFrom":makeQuery(id+"F3.boolean.opBoolean","COPY",EDGE,{"derivedFrom":makeQuery(id+"F3.opExtrude","SWEPT_EDGE",EDGE,{"disambiguationData":[OSD([sQuery(id+"F2.wireOp",EDGE,"E7.MirrorCS"),sQuery(id+"F2.wireOp",EDGE,"E8.MirrorCS")])]})}),"instanceName":"18"});
            var Q44;
            Q44=makeQuery(id+"F4.opPattern","COPY",EDGE,{"derivedFrom":makeQuery(id+"F3.boolean.opBoolean","COPY",EDGE,{"derivedFrom":makeQuery(id+"F3.opExtrude","SWEPT_EDGE",EDGE,{"disambiguationData":[OSD([sQuery(id+"F2.wireOp",EDGE,"E2"),sQuery(id+"F2.wireOp",EDGE,"E5")])]})}),"instanceName":"18"});
            var Q45;
            Q45=makeQuery(id+"F4.opPattern","COPY",EDGE,{"derivedFrom":makeQuery(id+"F3.boolean.opBoolean","COPY",EDGE,{"derivedFrom":makeQuery(id+"F3.opExtrude","SWEPT_EDGE",EDGE,{"disambiguationData":[OSD([sQuery(id+"F0.wireOp",EDGE,"E0"),sQuery(id+"F2.wireOp",EDGE,"E5")])]})}),"instanceName":"18"});
            fillet(context, id + "F8", {"entities" : qUnion([Q0, Q1, Q2, Q3, Q4, Q5, Q6, Q7, Q8, Q9, Q10, Q11, Q12, Q13, Q14, Q15, Q16, Q17, Q18, Q19, Q20, Q21, Q22, Q23, Q24, Q25, Q26, Q27, Q28, Q29, Q30, Q31, Q32, Q33, Q34, Q35, Q36, Q37, Q38, Q39, Q40, Q41, Q42, Q43, Q44, Q45]), "radius" : .15 * mm, "tangentPropagation" : true, "allowEdgeOverflow" : false});
        }
        {
            var Q0;
            Q0=makeQuery(id+"F1.opExtrude","CAP_FACE",FACE,{"disambiguationData":[OSD([sQuery(id+"F0.wireOp",EDGE,"E0")])],"isStart":false});
            var sketch = newSketch(context, id + "F9", { "sketchPlane" : qUnion([Q0])});
            skCircle(sketch, "E9", {"center": v(0, 0) * mm, "radius": 1 * mm});
            skLineSegment(sketch, "E10", {"start": v(0, 0) * mm, "end": v(0, 0.8) * mm});
            skLineSegment(sketch, "E11", {"start": v(0.6, 0.8) * mm, "end": v(-0.6, 0.8) * mm});
            skSolve(sketch);
        }
        {
            var Q0;
            {var subQ0=sQuery(id+"F9.wireOp",EDGE,"E11");var subQ4=makeQuery(id+"F9.imprint","IMPRINT",VERTEX,{"derivedFrom":subQ0});Q0=makeQuery(id+"F9.imprint","IMPRINT",FACE,{"disambiguationData":[TD([[makeQuery(id+"F9.imprint","IMPRINT",EDGE,{"disambiguationData":[TD([[subQ4,1.0]])],"derivedFrom":subQ0}),1.0]])]});}
            extrude(context, id + "F10", {"entities" : qUnion([Q0]), "operationType" : NewBodyOperationType.REMOVE, "oppositeDirection" : true, "depth" : 25 * mm, "offsetDistance" : 25 * mm});
        }
    });
